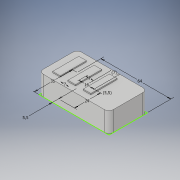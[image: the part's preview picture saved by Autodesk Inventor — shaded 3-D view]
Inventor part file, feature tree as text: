
AUTODESK INVENTOR PART (.ipt)
format: ipt  version: 2019 (Build 230136000, 136)  size: 133,120 bytes
history: native  units: mm
features: extrude x2, sketch x1, fillet x1
ambient origin geometry x8: Origin, YZ Plane, XZ Plane, XY Plane, X Axis, Y Axis, Z Axis, Center Point
bodies: Solid1 (feature_tree)
feature tree (4):
  sketch  "Sketch1"  dims[d0=35.0mm d1=64.0mm d2=7.0mm d3=7.0mm d4=24.0mm d5=5.5mm d6=5.5mm d7=30.0mm d9=14.0mm d10=10.0mm d12=10.0mm d14=7.0mm d15=18.0mm d16=0.0mm d17=19.0mm d18=0.0mm d19=4.0mm]
  extrude  "Extrusion1"  Depth=64.0mm
  extrude  "Extrusion2"  Depth=7.0mm
  fillet  "Fillet1"  Radius=7.0mm
